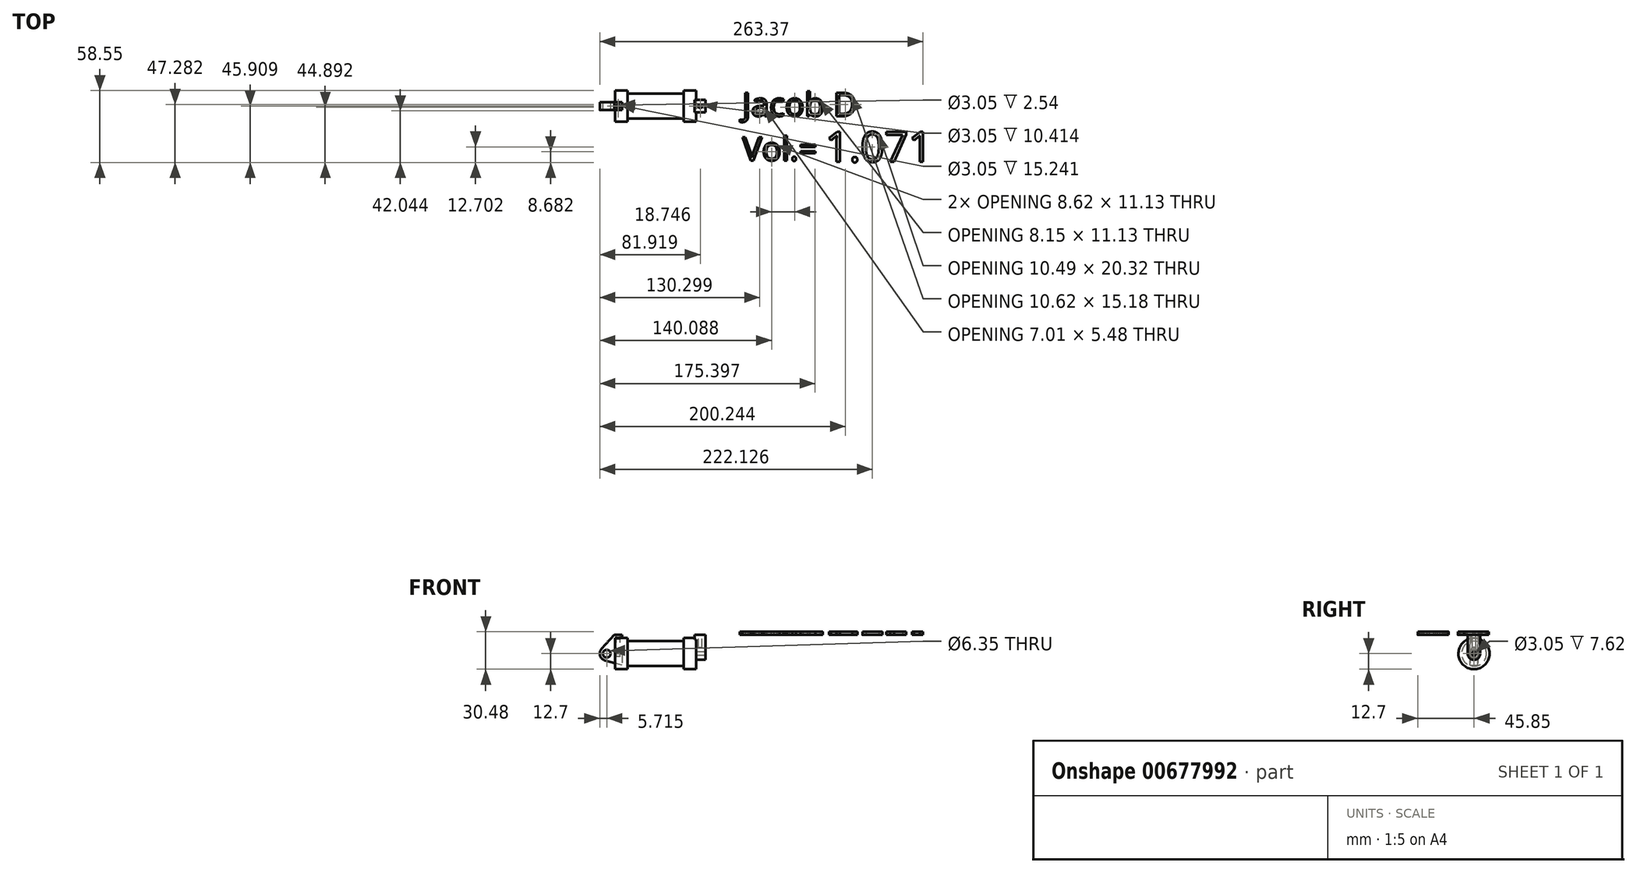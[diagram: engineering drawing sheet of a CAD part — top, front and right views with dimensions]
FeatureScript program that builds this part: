
annotation { "Feature Type Name" : "Feature", "Feature Type Description" : "" }
export const myFeature = defineFeature(function(context is Context, id is Id, definition is map)
    precondition{}
    {
        {
            var Q0;
            Q0=qCreatedBy(makeId("Front.planeOp"),FACE);
            var sketch = newSketch(context, id + "F0", { "sketchPlane" : qUnion([Q0])});
            skLineSegment(sketch, "E0", {"start": v(0, 0) * mm, "end": v(0, 12.7) * mm});
            skLineSegment(sketch, "E1", {"start": v(0, 12.7) * mm, "end": v(10.16, 12.7) * mm});
            skLineSegment(sketch, "E2", {"start": v(10.16, 12.7) * mm, "end": v(10.16, 10.16) * mm});
            skLineSegment(sketch, "E3", {"start": v(10.16, 10.16) * mm, "end": v(56.13, 10.16) * mm});
            skLineSegment(sketch, "E4", {"start": v(56.13, 10.16) * mm, "end": v(56.13, 12.7) * mm});
            skLineSegment(sketch, "E5", {"start": v(56.13, 12.7) * mm, "end": v(66.3, 12.7) * mm});
            skLineSegment(sketch, "E6", {"start": v(66.3, 12.7) * mm, "end": v(66.3, 0) * mm});
            skLineSegment(sketch, "E7", {"start": v(66.3, 0) * mm, "end": v(0, 0) * mm});
            skLineSegment(sketch, "E8", {"start": v(5.84, 15.24) * mm, "end": v(-0.5, 15.24) * mm});
            skLineSegment(sketch, "E9", {"start": v(-0.5, 15.24) * mm, "end": v(-10.88, 3.85) * mm});
            skLineSegment(sketch, "E10", {"start": v(0, 0) * mm, "end": v(-6.65, 0) * mm});
            skCircle(sketch, "E11", {"center": v(-6.65, 0) * mm, "radius": 5.72 * mm});
            skCircle(sketch, "E12", {"center": v(-6.65, 0) * mm, "radius": 3.18 * mm});
            skLineSegment(sketch, "E13", {"start": v(5.84, 15.24) * mm, "end": v(5.84, -9.4) * mm});
            skLineSegment(sketch, "E14", {"start": v(5.84, -9.4) * mm, "end": v(-8.18, -5.5) * mm});
            skSolve(sketch);
        }
        {
            var Q0;
            {var subQ0=sQuery(id+"F0.wireOp",EDGE,"E2");Q0=makeQuery(id+"F0.imprint","IMPRINT",FACE,{"disambiguationData":[TD([[makeQuery(id+"F0.imprint","IMPRINT",EDGE,{"derivedFrom":subQ0}),-1.0]])]});}
            var Q1;
            {var subQ0=sQuery(id+"F0.wireOp",EDGE,"E0");Q1=makeQuery(id+"F0.imprint","IMPRINT",FACE,{"disambiguationData":[TD([[makeQuery(id+"F0.imprint","IMPRINT",EDGE,{"derivedFrom":subQ0}),-1.0]])]});}
            var Q2;
            Q2=sQuery(id+"F0.wireOp",EDGE,"E7");
            revolve(context, id + "F1", {"entities" : qUnion([Q0, Q1]), "axis" : qUnion([Q2]), "revolveType" : RevolveType.FULL});
        }
        {
            var Q0;
            {var subQ1=sQuery(id+"F0.wireOp",EDGE,"E0");Q0=makeQuery(id+"F0.imprint","IMPRINT",FACE,{"disambiguationData":[TD([[makeQuery(id+"F0.imprint","IMPRINT",EDGE,{"derivedFrom":subQ1}),1.0]])]});}
            var Q1;
            {var subQ0=sQuery(id+"F0.wireOp",EDGE,"E14");Q1=makeQuery(id+"F0.imprint","IMPRINT",FACE,{"disambiguationData":[TD([[makeQuery(id+"F0.imprint","IMPRINT",EDGE,{"derivedFrom":subQ0}),-1.0]])]});}
            var Q2;
            {var subQ5=sQuery(id+"F0.wireOp",EDGE,"E12");Q2=makeQuery(id+"F0.imprint","IMPRINT",FACE,{"disambiguationData":[TD([[makeQuery(id+"F0.imprint","IMPRINT",EDGE,{"derivedFrom":subQ5}),-1.0]])]});}
            extrude(context, id + "F2", {"entities" : qUnion([Q0, Q1, Q2]), "endBound" : BoundingType.SYMMETRIC, "depth" : 6.35 * mm, "offsetDistance" : 25.4 * mm});
        }
        {
            var Q0;
            Q0=makeQuery(id+"F1.opRevolve","SWEPT_FACE",FACE,{"disambiguationData":[OSD([sQuery(id+"F0.wireOp",EDGE,"E6")])]});
            var sketch = newSketch(context, id + "F3", { "sketchPlane" : qUnion([Q0])});
            skCircle(sketch, "E15", {"center": v(0, 0) * mm, "radius": 1.52 * mm});
            skCircle(sketch, "E16", {"center": v(0, 0) * mm, "radius": 5.08 * mm});
            skLineSegment(sketch, "E17", {"start": v(-5.08, 0) * mm, "end": v(-5.08, 15.24) * mm});
            skLineSegment(sketch, "E18", {"start": v(5.08, 0) * mm, "end": v(5.08, 15.24) * mm});
            skLineSegment(sketch, "E19", {"start": v(-5.08, 15.24) * mm, "end": v(5.08, 15.24) * mm});
            skSolve(sketch);
        }
        {
            var Q0;
            Q0 = qSketchRegion(id + "F3", true);
            extrude(context, id + "F4", {"entities" : qUnion([Q0]), "operationType" : NewBodyOperationType.ADD, "depth" : 7.62 * mm, "offsetDistance" : 25.4 * mm, "hasSecondDirection" : true, "secondDirectionOppositeDirection" : true, "secondDirectionDepth" : 1.27 * mm});
        }
        {
            var Q0;
            Q0=makeQuery(id+"F2.opExtrude","SWEPT_FACE",FACE,{"disambiguationData":[OSD([sQuery(id+"F0.wireOp",EDGE,"E8")])]});
            var sketch = newSketch(context, id + "F5", { "sketchPlane" : qUnion([Q0])});
            skCircle(sketch, "E20", {"center": v(2.67, 0) * mm, "radius": 1.52 * mm});
            skCircle(sketch, "E21", {"center": v(69.55, 0.06) * mm, "radius": 1.52 * mm});
            skLineSegment(sketch, "E22", {"start": v(69.56, 0.07) * mm, "end": v(69.57, 0.06) * mm, "construction": true});
            skPoint(sketch, "E23", {"position": v(69.57, 0.06) * mm});
            skPoint(sketch, "E24.orphan", {"position": v(65.03, 5.08) * mm});
            skLineSegment(sketch, "E25.trimOffspring", {"start": v(69.55, 0.06) * mm, "end": v(69.56, 0.07) * mm, "construction": true});
            skPoint(sketch, "E26.trimOffspring.end.orphan", {"position": v(74.1, -4.97) * mm});
            skPoint(sketch, "E27.orphan", {"position": v(-0.5, 3.18) * mm});
            skPoint(sketch, "E28.end.orphan", {"position": v(5.84, -3.18) * mm});
            skText(sketch, "E29", { "text": "Jacob D\nVol.= ", "fontName": "OpenSans-Regular.ttf"});
            const initialGuessF5  = {"E29": [0.10383, -0.00807, 1, 0, 0.01917]};
            skSetInitialGuess(sketch, initialGuessF5);
            skSolve(sketch);
        }
        {
            var Q0;
            Q0=makeQuery(id+"F5.imprint","IMPRINT",FACE,{"disambiguationData":[TD([[makeQuery(id+"F5.imprint","IMPRINT",EDGE,{"derivedFrom":sQuery(id+"F5.wireOp",EDGE,"E21")}),1.0]])]});
            extrude(context, id + "F6", {"entities" : qUnion([Q0]), "operationType" : NewBodyOperationType.REMOVE, "oppositeDirection" : true, "depth" : 10.4 * mm, "offsetDistance" : 25.4 * mm});
        }
        {
            var Q0;
            Q0=makeQuery(id+"F5.imprint","IMPRINT",FACE,{"disambiguationData":[TD([[makeQuery(id+"F5.imprint","IMPRINT",EDGE,{"derivedFrom":sQuery(id+"F5.wireOp",EDGE,"E20")}),1.0]])]});
            extrude(context, id + "F7", {"entities" : qUnion([Q0]), "operationType" : NewBodyOperationType.REMOVE, "oppositeDirection" : true, "depth" : 17.78 * mm, "offsetDistance" : 25.4 * mm});
        }
        {
            var Q0;
            Q0=makeQuery(id+"F4.opExtrude","SWEPT_FACE",FACE,{"disambiguationData":[OSD([sQuery(id+"F3.wireOp",EDGE,"E19")])]});
            var sketch = newSketch(context, id + "F8", { "sketchPlane" : qUnion([Q0])});
            skText(sketch, "E30", { "text": "1.071", "fontName": "OpenSans-Regular.ttf"});
            const initialGuessF8  = {"E30": [0.17138, -0.04536, 1, 0, 0.0246]};
            skSetInitialGuess(sketch, initialGuessF8);
            skSolve(sketch);
        }
        {
            var Q0;
            Q0=makeQuery(id+"F5.imprint","IMPRINT",FACE,{"disambiguationData":[TD([[makeQuery(id+"F5.imprint","IMPRINT",EDGE,{"derivedFrom":sQuery(id+"F5.wireOp",EDGE,"E29.sketch_text.stroke-0")}),-1.0]])]});
            var Q1;
            Q1=makeQuery(id+"F5.imprint","IMPRINT",FACE,{"disambiguationData":[TD([[makeQuery(id+"F5.imprint","IMPRINT",EDGE,{"derivedFrom":sQuery(id+"F5.wireOp",EDGE,"E29.sketch_text.stroke-10")}),-1.0]])]});
            var Q2;
            Q2=makeQuery(id+"F5.imprint","IMPRINT",FACE,{"disambiguationData":[TD([[makeQuery(id+"F5.imprint","IMPRINT",EDGE,{"derivedFrom":sQuery(id+"F5.wireOp",EDGE,"E29.sketch_text.stroke-37")}),-1.0]])]});
            var Q3;
            Q3=makeQuery(id+"F5.imprint","IMPRINT",FACE,{"disambiguationData":[TD([[makeQuery(id+"F5.imprint","IMPRINT",EDGE,{"derivedFrom":sQuery(id+"F5.wireOp",EDGE,"E29.sketch_text.stroke-52")}),-1.0]])]});
            var Q4;
            Q4=makeQuery(id+"F5.imprint","IMPRINT",FACE,{"disambiguationData":[TD([[makeQuery(id+"F5.imprint","IMPRINT",EDGE,{"derivedFrom":sQuery(id+"F5.wireOp",EDGE,"E29.sketch_text.stroke-69")}),-1.0]])]});
            var Q5;
            Q5=makeQuery(id+"F5.imprint","IMPRINT",FACE,{"disambiguationData":[TD([[makeQuery(id+"F5.imprint","IMPRINT",EDGE,{"derivedFrom":sQuery(id+"F5.wireOp",EDGE,"E29.sketch_text.stroke-92")}),-1.0]])]});
            var Q6;
            Q6=makeQuery(id+"F5.imprint","IMPRINT",FACE,{"disambiguationData":[TD([[makeQuery(id+"F5.imprint","IMPRINT",EDGE,{"derivedFrom":sQuery(id+"F5.wireOp",EDGE,"E29.sketch_text.stroke-106")}),-1.0]])]});
            var Q7;
            Q7=makeQuery(id+"F5.imprint","IMPRINT",FACE,{"disambiguationData":[TD([[makeQuery(id+"F5.imprint","IMPRINT",EDGE,{"derivedFrom":sQuery(id+"F5.wireOp",EDGE,"E29.sketch_text.stroke-115")}),-1.0]])]});
            var Q8;
            Q8=makeQuery(id+"F5.imprint","IMPRINT",FACE,{"disambiguationData":[TD([[makeQuery(id+"F5.imprint","IMPRINT",EDGE,{"derivedFrom":sQuery(id+"F5.wireOp",EDGE,"E29.sketch_text.stroke-132")}),-1.0]])]});
            var Q9;
            Q9=makeQuery(id+"F5.imprint","IMPRINT",FACE,{"disambiguationData":[TD([[makeQuery(id+"F5.imprint","IMPRINT",EDGE,{"derivedFrom":sQuery(id+"F5.wireOp",EDGE,"E29.sketch_text.stroke-136")}),-1.0]])]});
            var Q10;
            Q10=makeQuery(id+"F5.imprint","IMPRINT",FACE,{"disambiguationData":[TD([[makeQuery(id+"F5.imprint","IMPRINT",EDGE,{"derivedFrom":sQuery(id+"F5.wireOp",EDGE,"E29.sketch_text.stroke-148")}),-1.0]])]});
            var Q11;
            Q11=makeQuery(id+"F5.imprint","IMPRINT",FACE,{"disambiguationData":[TD([[makeQuery(id+"F5.imprint","IMPRINT",EDGE,{"derivedFrom":sQuery(id+"F5.wireOp",EDGE,"E29.sketch_text.stroke-144")}),-1.0]])]});
            var Q12;
            Q12=makeQuery(id+"F8.imprint","IMPRINT",FACE,{"disambiguationData":[TD([[makeQuery(id+"F8.imprint","IMPRINT",EDGE,{"derivedFrom":sQuery(id+"F8.wireOp",EDGE,"E30.sketch_text.stroke-40")}),-1.0]])]});
            var Q13;
            Q13=makeQuery(id+"F8.imprint","IMPRINT",FACE,{"disambiguationData":[TD([[makeQuery(id+"F8.imprint","IMPRINT",EDGE,{"derivedFrom":sQuery(id+"F8.wireOp",EDGE,"E30.sketch_text.stroke-9")}),-1.0]])]});
            var Q14;
            Q14=makeQuery(id+"F8.imprint","IMPRINT",FACE,{"disambiguationData":[TD([[makeQuery(id+"F8.imprint","IMPRINT",EDGE,{"derivedFrom":sQuery(id+"F8.wireOp",EDGE,"E30.sketch_text.stroke-17")}),-1.0]])]});
            var Q15;
            Q15=makeQuery(id+"F8.imprint","IMPRINT",FACE,{"disambiguationData":[TD([[makeQuery(id+"F8.imprint","IMPRINT",EDGE,{"derivedFrom":sQuery(id+"F8.wireOp",EDGE,"E30.sketch_text.stroke-33")}),-1.0]])]});
            var Q16;
            Q16=makeQuery(id+"F8.imprint","IMPRINT",FACE,{"disambiguationData":[TD([[makeQuery(id+"F8.imprint","IMPRINT",EDGE,{"derivedFrom":sQuery(id+"F8.wireOp",EDGE,"E30.sketch_text.stroke-0")}),-1.0]])]});
            extrude(context, id + "F9", {"entities" : qUnion([Q0, Q1, Q2, Q3, Q4, Q5, Q6, Q7, Q8, Q9, Q10, Q11, Q12, Q13, Q14, Q15, Q16]), "depth" : 2.54 * mm, "offsetDistance" : 25.4 * mm});
        }
    });
